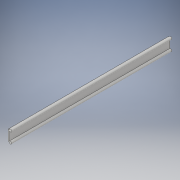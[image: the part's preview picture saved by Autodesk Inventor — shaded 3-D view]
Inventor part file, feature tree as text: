
AUTODESK INVENTOR PART (.ipt)
format: ipt  version: 2018 (Build 220112000, 112)  size: 109,568 bytes
history: native  units: in
note: dims shown in document units (in); Inventor stores cm internally (conversion verified against a paired STEP export)
features: extrude x2, sketch x2
ambient origin geometry x8: Origin, YZ Plane, XZ Plane, XY Plane, X Axis, Y Axis, Z Axis, Center Point
bodies: Solid1 (feature_tree)
feature tree (4):
  extrude  "Extrusion1"  Depth=1.568in
  extrude  "Extrusion2"  Depth=24.0in
  sketch  "Sketch1"  dims[d0=0.215in d1=1.568in]
  sketch  "Sketch2"  dims[d2=24.0in d3=0.0in d4=0.05in d5=0.1965in d6=24.0in d7=0.0in]
